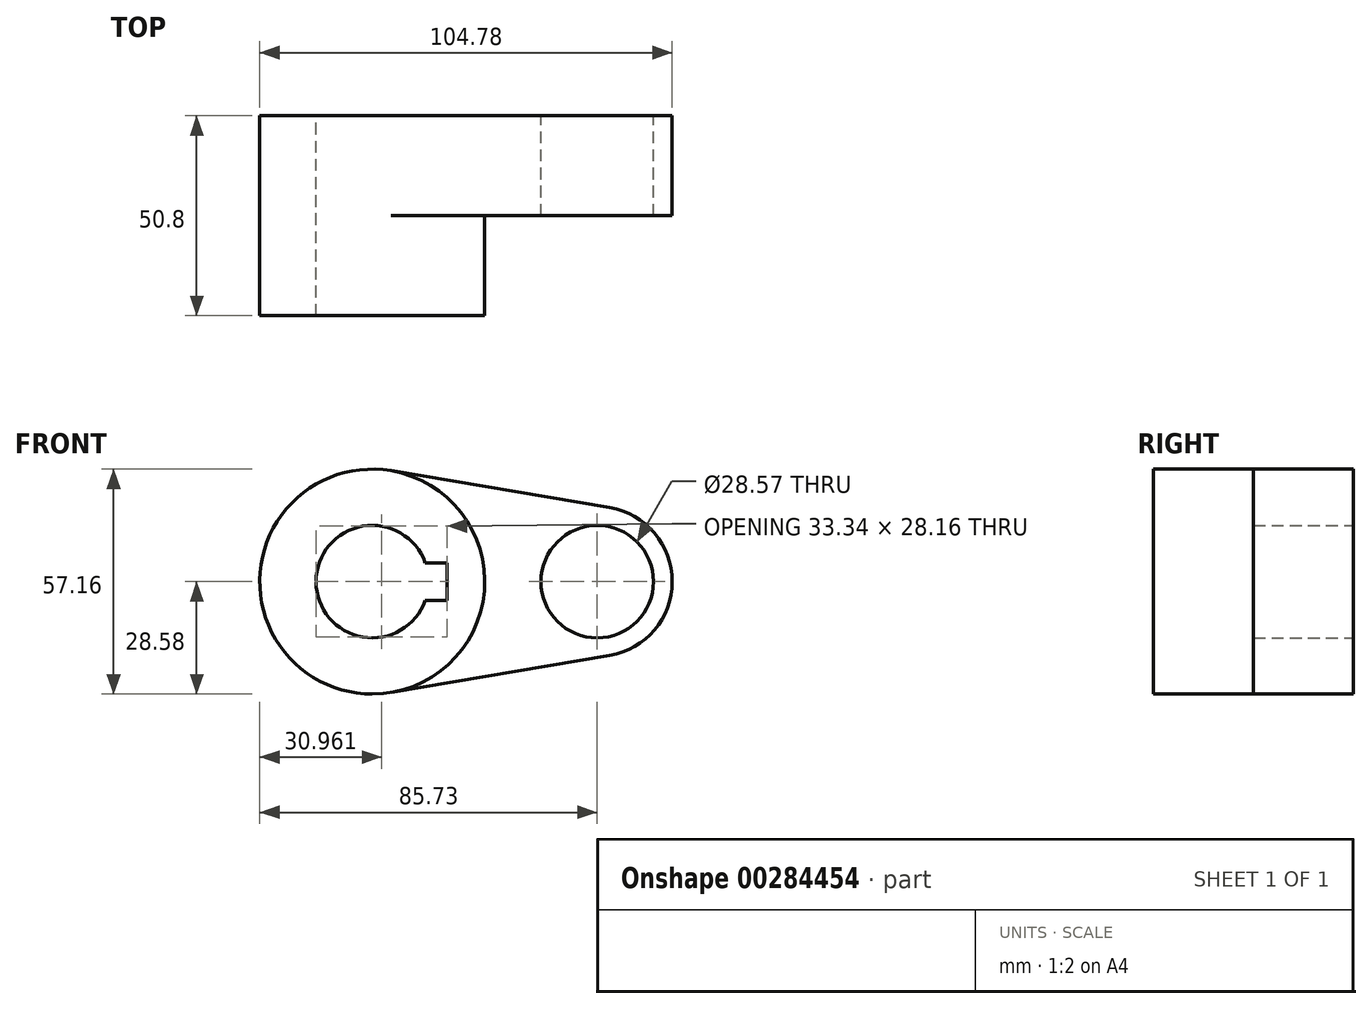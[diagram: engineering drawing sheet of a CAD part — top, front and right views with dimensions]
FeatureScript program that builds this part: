
annotation { "Feature Type Name" : "Feature", "Feature Type Description" : "" }
export const myFeature = defineFeature(function(context is Context, id is Id, definition is map)
    precondition{}
    {
        {
            var Q0;
            Q0=qCreatedBy(makeId("Front.planeOp"),FACE);
            var sketch = newSketch(context, id + "F0", { "sketchPlane" : qUnion([Q0])});
            skCircle(sketch, "E0", {"center": v(0, 0) * mm, "radius": 28.58 * mm});
            skCircle(sketch, "E1", {"center": v(57.15, 0) * mm, "radius": 19.05 * mm});
            skLineSegment(sketch, "E2", {"start": v(4.76, 28.18) * mm, "end": v(60.33, 18.78) * mm});
            skLineSegment(sketch, "E3", {"start": v(4.76, -28.18) * mm, "end": v(60.33, -18.78) * mm});
            skCircle(sketch, "E4", {"center": v(0, 0) * mm, "radius": 14.29 * mm});
            skCircle(sketch, "E5", {"center": v(57.15, 0) * mm, "radius": 14.29 * mm});
            skLineSegment(sketch, "E6.bottom", {"start": v(-19.05, 4.76) * mm, "end": v(19.05, 4.76) * mm});
            skLineSegment(sketch, "E6.top", {"start": v(-19.05, -4.76) * mm, "end": v(19.05, -4.76) * mm});
            skLineSegment(sketch, "E6.left", {"start": v(-19.05, 4.76) * mm, "end": v(-19.05, -4.76) * mm});
            skLineSegment(sketch, "E6.right", {"start": v(19.05, 4.76) * mm, "end": v(19.05, -4.76) * mm});
            skSolve(sketch);
        }
        {
            var Q0;
            {var subQ11=sQuery(id+"F0.wireOp",EDGE,"E6.left");Q0=makeQuery(id+"F0.imprint","IMPRINT",FACE,{"disambiguationData":[TD([[makeQuery(id+"F0.imprint","IMPRINT",EDGE,{"derivedFrom":subQ11}),-1.0]])]});}
            var Q1;
            {var subQ0=sQuery(id+"F0.wireOp",EDGE,"E2");Q1=makeQuery(id+"F0.imprint","IMPRINT",FACE,{"disambiguationData":[TD([[makeQuery(id+"F0.imprint","IMPRINT",EDGE,{"derivedFrom":subQ0}),-1.0]])]});}
            var Q2;
            Q2=makeQuery(id+"F0.imprint","IMPRINT",FACE,{"disambiguationData":[TD([[makeQuery(id+"F0.imprint","IMPRINT",EDGE,{"derivedFrom":sQuery(id+"F0.wireOp",EDGE,"E5")}),-1.0]])]});
            var Q3;
            {var subQ5=sQuery(id+"F0.wireOp",EDGE,"E6.left");Q3=makeQuery(id+"F0.imprint","IMPRINT",FACE,{"disambiguationData":[TD([[makeQuery(id+"F0.imprint","IMPRINT",EDGE,{"derivedFrom":subQ5}),1.0]])]});}
            extrude(context, id + "F1", {"entities" : qUnion([Q0, Q1, Q2, Q3]), "depth" : 25.4 * mm});
        }
        {
            var Q0;
            {var subQ11=sQuery(id+"F0.wireOp",EDGE,"E6.left");Q0=makeQuery(id+"F0.imprint","IMPRINT",FACE,{"disambiguationData":[TD([[makeQuery(id+"F0.imprint","IMPRINT",EDGE,{"derivedFrom":subQ11}),-1.0]])]});}
            var Q1;
            {var subQ5=sQuery(id+"F0.wireOp",EDGE,"E6.left");Q1=makeQuery(id+"F0.imprint","IMPRINT",FACE,{"disambiguationData":[TD([[makeQuery(id+"F0.imprint","IMPRINT",EDGE,{"derivedFrom":subQ5}),1.0]])]});}
            extrude(context, id + "F2", {"entities" : qUnion([Q0, Q1]), "operationType" : NewBodyOperationType.ADD, "depth" : 50.8 * mm});
        }
    });
